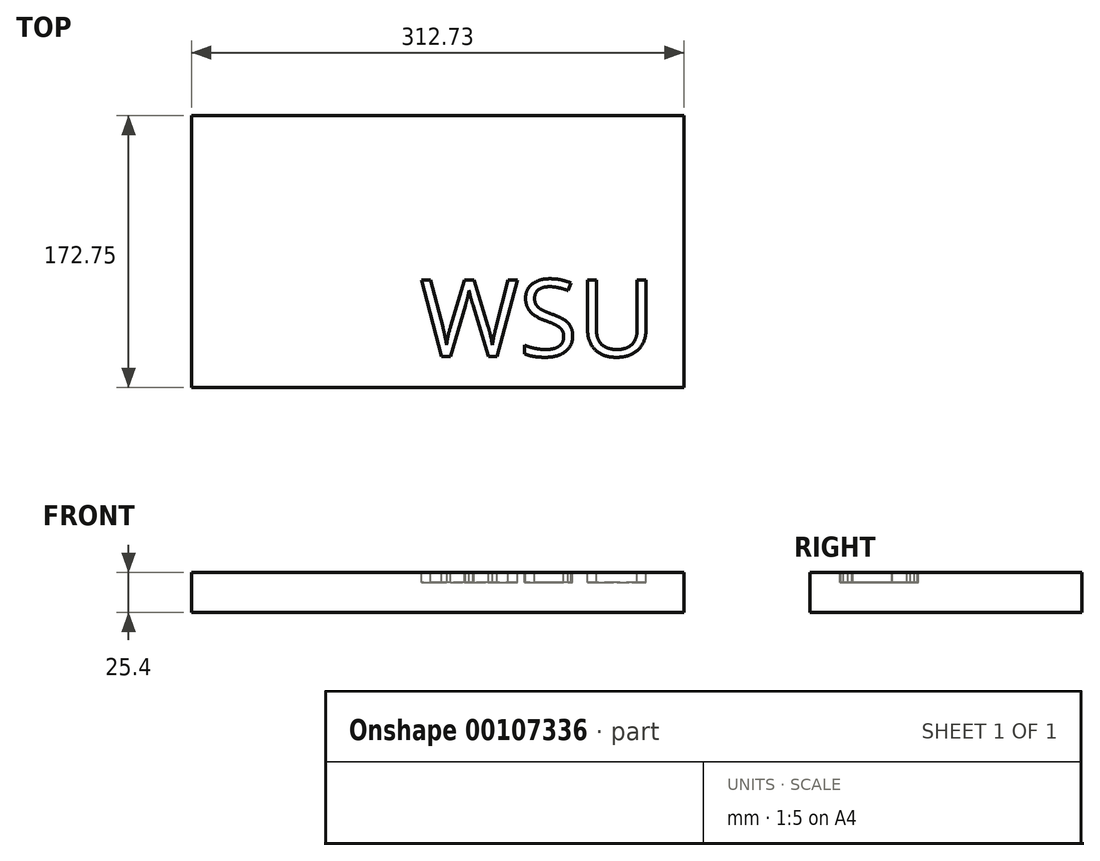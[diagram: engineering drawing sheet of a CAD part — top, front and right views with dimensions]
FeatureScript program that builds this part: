
annotation { "Feature Type Name" : "Feature", "Feature Type Description" : "" }
export const myFeature = defineFeature(function(context is Context, id is Id, definition is map)
    precondition{}
    {
        {
            var Q0;
            Q0=qCreatedBy(makeId("Top.planeOp"),FACE);
            var sketch = newSketch(context, id + "F0", { "sketchPlane" : qUnion([Q0])});
            skLineSegment(sketch, "E0.bottom", {"start": v(-154.98, 84.94) * mm, "end": v(157.75, 84.94) * mm});
            skLineSegment(sketch, "E0.top", {"start": v(-154.98, -87.81) * mm, "end": v(157.75, -87.81) * mm});
            skLineSegment(sketch, "E0.left", {"start": v(-154.98, 84.94) * mm, "end": v(-154.98, -87.81) * mm});
            skLineSegment(sketch, "E0.right", {"start": v(157.75, 84.94) * mm, "end": v(157.75, -87.81) * mm});
            skSolve(sketch);
        }
        {
            var Q0;
            Q0=makeQuery(id+"F0.imprint","IMPRINT",FACE,{"disambiguationData":[TD([[makeQuery(id+"F0.imprint","IMPRINT",EDGE,{"derivedFrom":sQuery(id+"F0.wireOp",EDGE,"E0.bottom")}),-1.0]])]});
            extrude(context, id + "F1", {"entities" : qUnion([Q0]), "depth" : 25.4 * mm});
        }
        {
            var Q0;
            Q0=makeQuery(id+"F1.opExtrude","CAP_FACE",FACE,{"disambiguationData":[OSD([sQuery(id+"F0.wireOp",EDGE,"E0.bottom"),sQuery(id+"F0.wireOp",EDGE,"E0.top"),sQuery(id+"F0.wireOp",EDGE,"E0.left"),sQuery(id+"F0.wireOp",EDGE,"E0.right")])],"isStart":false});
            var sketch = newSketch(context, id + "F2", { "sketchPlane" : qUnion([Q0])});
            skText(sketch, "E1", { "text": "WSU\n", "fontName": "OpenSans-Regular.ttf"});
            const initialGuessF2  = {"E1": [0.11707, 0.1098, 1, 0, 0.04896]};
            skSetInitialGuess(sketch, initialGuessF2);
            skSolve(sketch);
        }
        {
            var Q0;
            Q0 = qSketchRegion(id + "F2", true);
            extrude(context, id + "F3", {"entities" : qUnion([Q0]), "oppositeDirection" : true, "depth" : 6.35 * mm});
        }
        {
            var Q0;
            Q0=makeQuery(id+"F3.opExtrude","SWEPT_BODY",BODY,{"disambiguationData":[OSD([sQuery(id+"F2.wireOp",EDGE,"E1.sketch_text.stroke-0"),sQuery(id+"F2.wireOp",EDGE,"E1.sketch_text.stroke-1"),sQuery(id+"F2.wireOp",EDGE,"E1.sketch_text.stroke-2"),sQuery(id+"F2.wireOp",EDGE,"E1.sketch_text.stroke-3"),sQuery(id+"F2.wireOp",EDGE,"E1.sketch_text.stroke-4"),sQuery(id+"F2.wireOp",EDGE,"E1.sketch_text.stroke-5"),sQuery(id+"F2.wireOp",EDGE,"E1.sketch_text.stroke-6"),sQuery(id+"F2.wireOp",EDGE,"E1.sketch_text.stroke-7"),sQuery(id+"F2.wireOp",EDGE,"E1.sketch_text.stroke-8"),sQuery(id+"F2.wireOp",EDGE,"E1.sketch_text.stroke-9"),sQuery(id+"F2.wireOp",EDGE,"E1.sketch_text.stroke-10"),sQuery(id+"F2.wireOp",EDGE,"E1.sketch_text.stroke-11"),sQuery(id+"F2.wireOp",EDGE,"E1.sketch_text.stroke-12"),sQuery(id+"F2.wireOp",EDGE,"E1.sketch_text.stroke-13"),sQuery(id+"F2.wireOp",EDGE,"E1.sketch_text.stroke-14"),sQuery(id+"F2.wireOp",EDGE,"E1.sketch_text.stroke-15"),sQuery(id+"F2.wireOp",EDGE,"E1.sketch_text.stroke-16"),sQuery(id+"F2.wireOp",EDGE,"E1.sketch_text.stroke-17"),sQuery(id+"F2.wireOp",EDGE,"E1.sketch_text.stroke-18"),sQuery(id+"F2.wireOp",EDGE,"E1.sketch_text.stroke-19")])]});
            var Q1;
            Q1=makeQuery(id+"F3.opExtrude","SWEPT_BODY",BODY,{"disambiguationData":[OSD([sQuery(id+"F2.wireOp",EDGE,"E1.sketch_text.stroke-20"),sQuery(id+"F2.wireOp",EDGE,"E1.sketch_text.stroke-21"),sQuery(id+"F2.wireOp",EDGE,"E1.sketch_text.stroke-22"),sQuery(id+"F2.wireOp",EDGE,"E1.sketch_text.stroke-23"),sQuery(id+"F2.wireOp",EDGE,"E1.sketch_text.stroke-24"),sQuery(id+"F2.wireOp",EDGE,"E1.sketch_text.stroke-25"),sQuery(id+"F2.wireOp",EDGE,"E1.sketch_text.stroke-26"),sQuery(id+"F2.wireOp",EDGE,"E1.sketch_text.stroke-27"),sQuery(id+"F2.wireOp",EDGE,"E1.sketch_text.stroke-28"),sQuery(id+"F2.wireOp",EDGE,"E1.sketch_text.stroke-29"),sQuery(id+"F2.wireOp",EDGE,"E1.sketch_text.stroke-30"),sQuery(id+"F2.wireOp",EDGE,"E1.sketch_text.stroke-31"),sQuery(id+"F2.wireOp",EDGE,"E1.sketch_text.stroke-32"),sQuery(id+"F2.wireOp",EDGE,"E1.sketch_text.stroke-33"),sQuery(id+"F2.wireOp",EDGE,"E1.sketch_text.stroke-34"),sQuery(id+"F2.wireOp",EDGE,"E1.sketch_text.stroke-35"),sQuery(id+"F2.wireOp",EDGE,"E1.sketch_text.stroke-36"),sQuery(id+"F2.wireOp",EDGE,"E1.sketch_text.stroke-37"),sQuery(id+"F2.wireOp",EDGE,"E1.sketch_text.stroke-38"),sQuery(id+"F2.wireOp",EDGE,"E1.sketch_text.stroke-39"),sQuery(id+"F2.wireOp",EDGE,"E1.sketch_text.stroke-40"),sQuery(id+"F2.wireOp",EDGE,"E1.sketch_text.stroke-41"),sQuery(id+"F2.wireOp",EDGE,"E1.sketch_text.stroke-42"),sQuery(id+"F2.wireOp",EDGE,"E1.sketch_text.stroke-43"),sQuery(id+"F2.wireOp",EDGE,"E1.sketch_text.stroke-44")])]});
            var Q2;
            Q2=makeQuery(id+"F3.opExtrude","SWEPT_BODY",BODY,{"disambiguationData":[OSD([sQuery(id+"F2.wireOp",EDGE,"E1.sketch_text.stroke-45"),sQuery(id+"F2.wireOp",EDGE,"E1.sketch_text.stroke-46"),sQuery(id+"F2.wireOp",EDGE,"E1.sketch_text.stroke-47"),sQuery(id+"F2.wireOp",EDGE,"E1.sketch_text.stroke-48"),sQuery(id+"F2.wireOp",EDGE,"E1.sketch_text.stroke-49"),sQuery(id+"F2.wireOp",EDGE,"E1.sketch_text.stroke-50"),sQuery(id+"F2.wireOp",EDGE,"E1.sketch_text.stroke-51"),sQuery(id+"F2.wireOp",EDGE,"E1.sketch_text.stroke-52"),sQuery(id+"F2.wireOp",EDGE,"E1.sketch_text.stroke-53"),sQuery(id+"F2.wireOp",EDGE,"E1.sketch_text.stroke-54"),sQuery(id+"F2.wireOp",EDGE,"E1.sketch_text.stroke-55"),sQuery(id+"F2.wireOp",EDGE,"E1.sketch_text.stroke-56"),sQuery(id+"F2.wireOp",EDGE,"E1.sketch_text.stroke-57"),sQuery(id+"F2.wireOp",EDGE,"E1.sketch_text.stroke-58")])]});
            transform(context, id + "F4", {"entities" : qUnion([Q0, Q1, Q2]), "transformType" : TransformType.TRANSLATION_3D, "dx" : -127 * mm, "dy" : -177.8 * mm, "dz" : 0 * mm, "makeCopy" : false});
        }
        {
            var Q0;
            Q0=makeQuery(id+"F3.opExtrude","SWEPT_BODY",BODY,{"disambiguationData":[OSD([sQuery(id+"F2.wireOp",EDGE,"E1.sketch_text.stroke-20"),sQuery(id+"F2.wireOp",EDGE,"E1.sketch_text.stroke-21"),sQuery(id+"F2.wireOp",EDGE,"E1.sketch_text.stroke-22"),sQuery(id+"F2.wireOp",EDGE,"E1.sketch_text.stroke-23"),sQuery(id+"F2.wireOp",EDGE,"E1.sketch_text.stroke-24"),sQuery(id+"F2.wireOp",EDGE,"E1.sketch_text.stroke-25"),sQuery(id+"F2.wireOp",EDGE,"E1.sketch_text.stroke-26"),sQuery(id+"F2.wireOp",EDGE,"E1.sketch_text.stroke-27"),sQuery(id+"F2.wireOp",EDGE,"E1.sketch_text.stroke-28"),sQuery(id+"F2.wireOp",EDGE,"E1.sketch_text.stroke-29"),sQuery(id+"F2.wireOp",EDGE,"E1.sketch_text.stroke-30"),sQuery(id+"F2.wireOp",EDGE,"E1.sketch_text.stroke-31"),sQuery(id+"F2.wireOp",EDGE,"E1.sketch_text.stroke-32"),sQuery(id+"F2.wireOp",EDGE,"E1.sketch_text.stroke-33"),sQuery(id+"F2.wireOp",EDGE,"E1.sketch_text.stroke-34"),sQuery(id+"F2.wireOp",EDGE,"E1.sketch_text.stroke-35"),sQuery(id+"F2.wireOp",EDGE,"E1.sketch_text.stroke-36"),sQuery(id+"F2.wireOp",EDGE,"E1.sketch_text.stroke-37"),sQuery(id+"F2.wireOp",EDGE,"E1.sketch_text.stroke-38"),sQuery(id+"F2.wireOp",EDGE,"E1.sketch_text.stroke-39"),sQuery(id+"F2.wireOp",EDGE,"E1.sketch_text.stroke-40"),sQuery(id+"F2.wireOp",EDGE,"E1.sketch_text.stroke-41"),sQuery(id+"F2.wireOp",EDGE,"E1.sketch_text.stroke-42"),sQuery(id+"F2.wireOp",EDGE,"E1.sketch_text.stroke-43"),sQuery(id+"F2.wireOp",EDGE,"E1.sketch_text.stroke-44")])]});
            var Q1;
            Q1=makeQuery(id+"F3.opExtrude","SWEPT_BODY",BODY,{"disambiguationData":[OSD([sQuery(id+"F2.wireOp",EDGE,"E1.sketch_text.stroke-45"),sQuery(id+"F2.wireOp",EDGE,"E1.sketch_text.stroke-46"),sQuery(id+"F2.wireOp",EDGE,"E1.sketch_text.stroke-47"),sQuery(id+"F2.wireOp",EDGE,"E1.sketch_text.stroke-48"),sQuery(id+"F2.wireOp",EDGE,"E1.sketch_text.stroke-49"),sQuery(id+"F2.wireOp",EDGE,"E1.sketch_text.stroke-50"),sQuery(id+"F2.wireOp",EDGE,"E1.sketch_text.stroke-51"),sQuery(id+"F2.wireOp",EDGE,"E1.sketch_text.stroke-52"),sQuery(id+"F2.wireOp",EDGE,"E1.sketch_text.stroke-53"),sQuery(id+"F2.wireOp",EDGE,"E1.sketch_text.stroke-54"),sQuery(id+"F2.wireOp",EDGE,"E1.sketch_text.stroke-55"),sQuery(id+"F2.wireOp",EDGE,"E1.sketch_text.stroke-56"),sQuery(id+"F2.wireOp",EDGE,"E1.sketch_text.stroke-57"),sQuery(id+"F2.wireOp",EDGE,"E1.sketch_text.stroke-58")])]});
            var Q2;
            Q2=makeQuery(id+"F3.opExtrude","SWEPT_BODY",BODY,{"disambiguationData":[OSD([sQuery(id+"F2.wireOp",EDGE,"E1.sketch_text.stroke-0"),sQuery(id+"F2.wireOp",EDGE,"E1.sketch_text.stroke-1"),sQuery(id+"F2.wireOp",EDGE,"E1.sketch_text.stroke-2"),sQuery(id+"F2.wireOp",EDGE,"E1.sketch_text.stroke-3"),sQuery(id+"F2.wireOp",EDGE,"E1.sketch_text.stroke-4"),sQuery(id+"F2.wireOp",EDGE,"E1.sketch_text.stroke-5"),sQuery(id+"F2.wireOp",EDGE,"E1.sketch_text.stroke-6"),sQuery(id+"F2.wireOp",EDGE,"E1.sketch_text.stroke-7"),sQuery(id+"F2.wireOp",EDGE,"E1.sketch_text.stroke-8"),sQuery(id+"F2.wireOp",EDGE,"E1.sketch_text.stroke-9"),sQuery(id+"F2.wireOp",EDGE,"E1.sketch_text.stroke-10"),sQuery(id+"F2.wireOp",EDGE,"E1.sketch_text.stroke-11"),sQuery(id+"F2.wireOp",EDGE,"E1.sketch_text.stroke-12"),sQuery(id+"F2.wireOp",EDGE,"E1.sketch_text.stroke-13"),sQuery(id+"F2.wireOp",EDGE,"E1.sketch_text.stroke-14"),sQuery(id+"F2.wireOp",EDGE,"E1.sketch_text.stroke-15"),sQuery(id+"F2.wireOp",EDGE,"E1.sketch_text.stroke-16"),sQuery(id+"F2.wireOp",EDGE,"E1.sketch_text.stroke-17"),sQuery(id+"F2.wireOp",EDGE,"E1.sketch_text.stroke-18"),sQuery(id+"F2.wireOp",EDGE,"E1.sketch_text.stroke-19")])]});
            var Q3;
            Q3=makeQuery(id+"F1.opExtrude","SWEPT_BODY",BODY,{"disambiguationData":[OSD([sQuery(id+"F0.wireOp",EDGE,"E0.bottom"),sQuery(id+"F0.wireOp",EDGE,"E0.top"),sQuery(id+"F0.wireOp",EDGE,"E0.left"),sQuery(id+"F0.wireOp",EDGE,"E0.right")])]});
            booleanBodies(context, id + "F5", {"operationType" : BooleanOperationType.SUBTRACTION, "tools" : qUnion([Q0, Q1, Q2]), "targets" : qUnion([Q3])});
        }
    });
